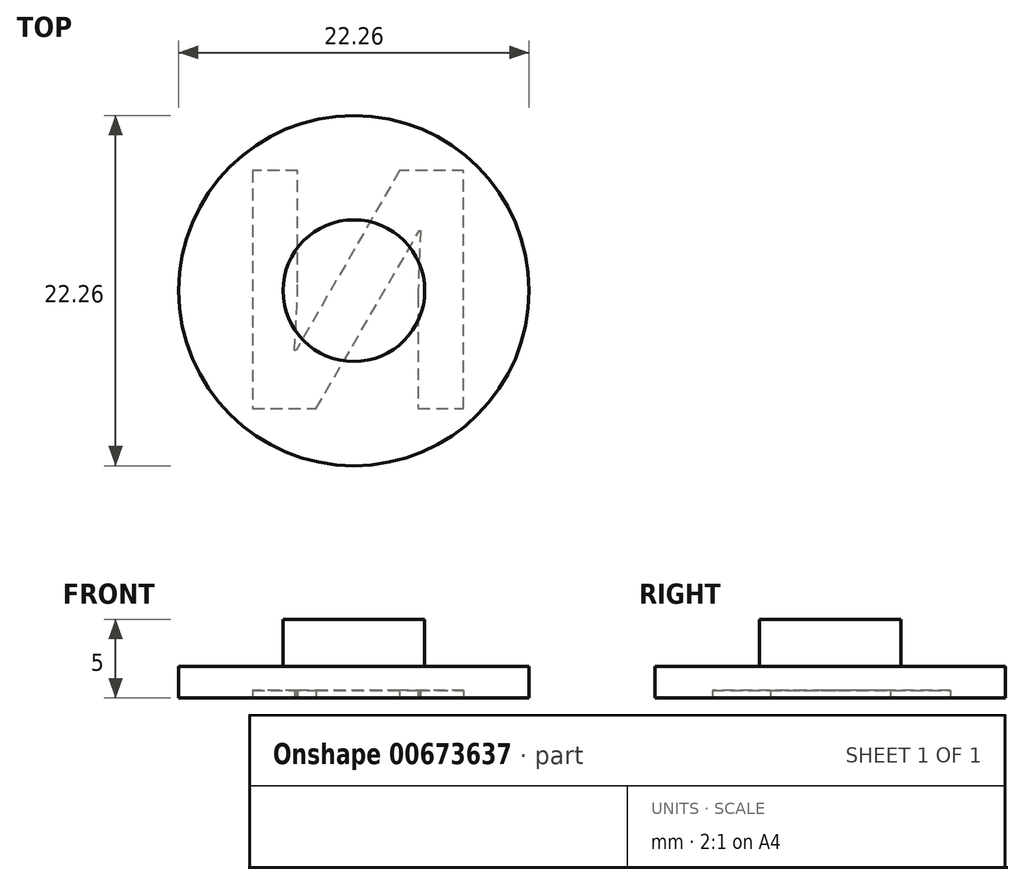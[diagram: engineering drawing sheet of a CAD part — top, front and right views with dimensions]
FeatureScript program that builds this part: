
annotation { "Feature Type Name" : "Feature", "Feature Type Description" : "" }
export const myFeature = defineFeature(function(context is Context, id is Id, definition is map)
    precondition{}
    {
        {
            var Q0;
            Q0=qCreatedBy(makeId("Top.planeOp"),FACE);
            var sketch = newSketch(context, id + "F0", { "sketchPlane" : qUnion([Q0])});
            skCircle(sketch, "E0", {"center": v(0, 0) * mm, "radius": 4.5 * mm});
            skSolve(sketch);
        }
        {
            var Q0;
            Q0=makeQuery(id+"F0.imprint","IMPRINT",FACE,{"disambiguationData":[TD([[makeQuery(id+"F0.imprint","IMPRINT",EDGE,{"derivedFrom":sQuery(id+"F0.wireOp",EDGE,"E0")}),1.0]])]});
            extrude(context, id + "F1", {"entities" : qUnion([Q0]), "depth" : 3 * mm, "offsetDistance" : 25.4 * mm});
        }
        {
            var Q0;
            Q0=qCreatedBy(makeId("Top.planeOp"),FACE);
            var sketch = newSketch(context, id + "F2", { "sketchPlane" : qUnion([Q0])});
            skCircle(sketch, "E1", {"center": v(0, 0) * mm, "radius": 11.12 * mm});
            skSolve(sketch);
        }
        {
            var Q0;
            Q0=makeQuery(id+"F2.imprint","IMPRINT",FACE,{"disambiguationData":[TD([[makeQuery(id+"F2.imprint","IMPRINT",EDGE,{"derivedFrom":sQuery(id+"F2.wireOp",EDGE,"E1")}),1.0]])]});
            extrude(context, id + "F3", {"entities" : qUnion([Q0]), "operationType" : NewBodyOperationType.ADD, "oppositeDirection" : true, "depth" : 2 * mm, "offsetDistance" : 25.4 * mm});
        }
        {
            var Q0;
            Q0=makeQuery(id+"F3.opExtrude","CAP_FACE",FACE,{"disambiguationData":[OSD([sQuery(id+"F2.wireOp",EDGE,"E1")])],"isStart":false});
            var sketch = newSketch(context, id + "F4", { "sketchPlane" : qUnion([Q0])});
            skText(sketch, "E2", { "text": "N", "fontName": "OpenSans-Bold.ttf"});
            skLineSegment(sketch, "E3", {"start": v(-8.34, 7.62) * mm, "end": v(8.34, -7.62) * mm, "construction": true});
            skLineSegment(sketch, "E4", {"start": v(8.34, 7.62) * mm, "end": v(-8.34, -7.62) * mm, "construction": true});
            skPoint(sketch, "E5", {"position": v(0, 0) * mm});
            const initialGuessF4  = {"E2": [-0.00834, -0.00762, 1, 0, 0.01524]};
            skSetInitialGuess(sketch, initialGuessF4);
            skSolve(sketch);
        }
        {
            var Q0;
            Q0 = qSketchRegion(id + "F4", true);
            extrude(context, id + "F5", {"entities" : qUnion([Q0]), "operationType" : NewBodyOperationType.REMOVE, "oppositeDirection" : true, "depth" : .5 * mm, "offsetDistance" : 25.4 * mm});
        }
    });
